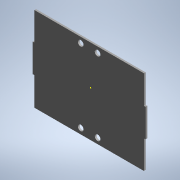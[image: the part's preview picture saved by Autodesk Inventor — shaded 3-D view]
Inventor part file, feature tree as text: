
AUTODESK INVENTOR PART (.ipt)
format: ipt  version: 2020 (Build 240168000, 168)  size: 137,728 bytes
history: native  units: mm (DEFAULTED — no unit token found)
features: sketch x10, extrude x8
ambient origin geometry x8: Origin, YZ Plane, XZ Plane, XY Plane, X Axis, Y Axis, Z Axis, Center Point
bodies: Solid1 (feature_tree)
feature tree (18):
  extrude  "Extrusion1"  Depth=3.0mm TaperAngle=0.0deg
  sketch  "Sketch2"  dims[d17=3.0mm d18=50.0mm]
  sketch  "Sketch3"  dims[d19=3.0mm d20=0.0mm d21=50.0mm]
  extrude  "Extrusion2"  Depth=50.0mm
  extrude  "Extrusion3"  Depth=50.0mm
  extrude  "Extrusion4"  Depth=3.0mm TaperAngle=0.0deg
  extrude  "Extrusion5"  Depth=3.0mm
  extrude  "Extrusion6"  Depth=3.0mm
  extrude  "Extrusion7"  Depth=3.0mm TaperAngle=0.0deg
  extrude  "Extrusion8"  Depth=24.75mm TaperAngle=0.0deg
  sketch  "Sketch1"  dims[d2=3.0mm d3=0.0mm d15=3.0mm d16=0.0mm]
  sketch  "Sketch4"  dims[d22=3.0mm d23=3.0mm d24=0.0mm]
  sketch  "Sketch5"  dims[d25=50.0mm d26=3.0mm]
  sketch  "Sketch6"  dims[d27=3.0mm d28=0.0mm d32=15.0mm]
  sketch  "Sketch7"  dims[d33=30.0mm d34=3.0mm d35=0.0mm]
  sketch  "Sketch8"  dims[d36=30.0mm d37=0.0mm d48=24.75mm d49=0.0mm]
  sketch  "Sketch9"
  sketch  "Sketch10"
